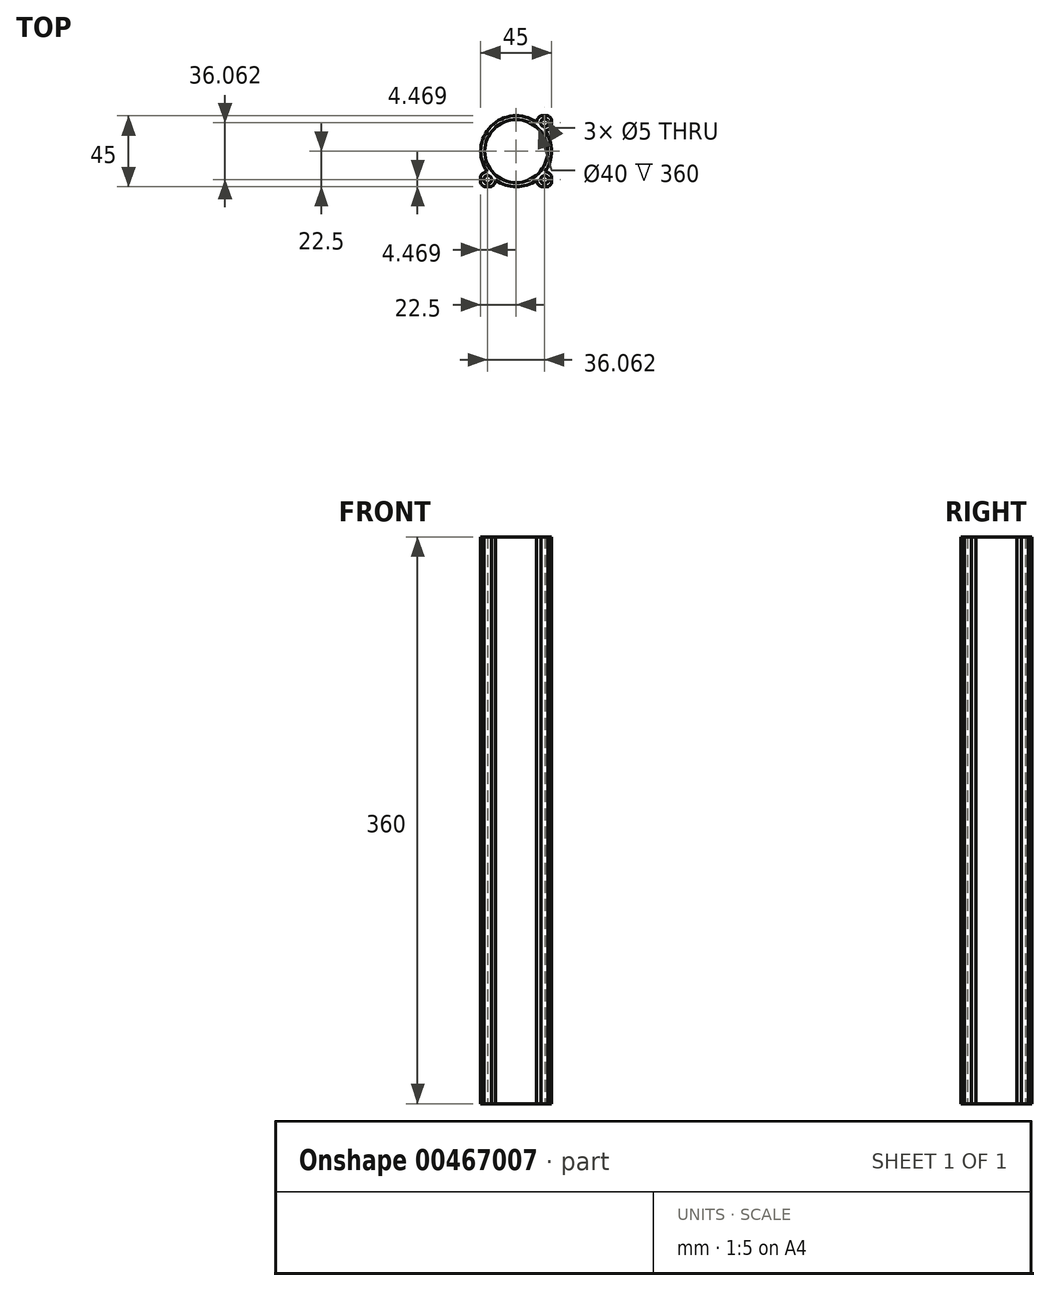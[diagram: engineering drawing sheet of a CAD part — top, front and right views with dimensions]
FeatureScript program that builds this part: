
annotation { "Feature Type Name" : "Feature", "Feature Type Description" : "" }
export const myFeature = defineFeature(function(context is Context, id is Id, definition is map)
    precondition{}
    {
        {
            var Q0;
            Q0=qCreatedBy(makeId("Top.planeOp"),FACE);
            var sketch = newSketch(context, id + "F0", { "sketchPlane" : qUnion([Q0])});
            skCircle(sketch, "E0", {"center": v(0, 0) * mm, "radius": 22.5 * mm});
            skLineSegment(sketch, "E1", {"start": v(0, 0) * mm, "end": v(22.5, 0) * mm});
            skLineSegment(sketch, "E2", {"start": v(22.5, 0) * mm, "end": v(22.5, 22.5) * mm});
            skLineSegment(sketch, "E3.bottom", {"start": v(22.5, 22.5) * mm, "end": v(-22.5, 22.5) * mm});
            skLineSegment(sketch, "E3.top", {"start": v(22.5, -22.5) * mm, "end": v(-22.5, -22.5) * mm});
            skLineSegment(sketch, "E3.left", {"start": v(22.5, 22.5) * mm, "end": v(22.5, -22.5) * mm});
            skLineSegment(sketch, "E3.right", {"start": v(-22.5, 22.5) * mm, "end": v(-22.5, -22.5) * mm});
            skLineSegment(sketch, "E4", {"start": v(-22.5, 22.5) * mm, "end": v(0, 0) * mm});
            skLineSegment(sketch, "E5", {"start": v(0, 0) * mm, "end": v(22.5, 22.5) * mm});
            skLineSegment(sketch, "E6", {"start": v(0, 0) * mm, "end": v(22.5, -22.5) * mm});
            skLineSegment(sketch, "E7", {"start": v(0, 0) * mm, "end": v(-22.5, -22.5) * mm});
            skLineSegment(sketch, "E8", {"start": v(-15.9, 15.9) * mm, "end": v(-18.03, 18.03) * mm});
            skCircle(sketch, "E9", {"center": v(-18.03, 18.03) * mm, "radius": 5 * mm});
            skCircle(sketch, "E10.MirrorC", {"center": v(18.03, -18.03) * mm, "radius": 5 * mm});
            skCircle(sketch, "E11.MirrorC", {"center": v(18.03, 18.03) * mm, "radius": 5 * mm});
            skCircle(sketch, "E12.MirrorC", {"center": v(-18.03, -18.03) * mm, "radius": 5 * mm});
            skSolve(sketch);
        }
        {
            var Q0;
            {var subQ6=sQuery(id+"F0.wireOp",EDGE,"E0");var subQ10=makeQuery(id+"F0.imprint","INTERSECT",VERTEX,{"derivedFrom":[subQ6,sQuery(id+"F0.wireOp",EDGE,"E3.right")]});Q0=makeQuery(id+"F0.imprint","IMPRINT",FACE,{"disambiguationData":[TD([[makeQuery(id+"F0.imprint","IMPRINT",EDGE,{"disambiguationData":[TD([[subQ10,1.0]])],"derivedFrom":subQ6}),1.0]])]});}
            var Q1;
            {var subQ7=sQuery(id+"F0.wireOp",EDGE,"E0");var subQ8=makeQuery(id+"F0.imprint","INTERSECT",VERTEX,{"derivedFrom":[subQ7,sQuery(id+"F0.wireOp",EDGE,"E3.bottom")]});Q1=makeQuery(id+"F0.imprint","IMPRINT",FACE,{"disambiguationData":[TD([[makeQuery(id+"F0.imprint","IMPRINT",EDGE,{"disambiguationData":[TD([[subQ8,1.0]])],"derivedFrom":subQ7}),1.0]])]});}
            var Q2;
            {var subQ0=sQuery(id+"F0.wireOp",EDGE,"E1");Q2=makeQuery(id+"F0.imprint","IMPRINT",FACE,{"disambiguationData":[TD([[makeQuery(id+"F0.imprint","IMPRINT",EDGE,{"derivedFrom":subQ0}),1.0]])]});}
            var Q3;
            {var subQ0=sQuery(id+"F0.wireOp",EDGE,"E1");Q3=makeQuery(id+"F0.imprint","IMPRINT",FACE,{"disambiguationData":[TD([[makeQuery(id+"F0.imprint","IMPRINT",EDGE,{"derivedFrom":subQ0}),-1.0]])]});}
            var Q4;
            {var subQ7=sQuery(id+"F0.wireOp",EDGE,"E0");var subQ8=makeQuery(id+"F0.imprint","INTERSECT",VERTEX,{"derivedFrom":[subQ7,sQuery(id+"F0.wireOp",EDGE,"E3.top")]});Q4=makeQuery(id+"F0.imprint","IMPRINT",FACE,{"disambiguationData":[TD([[makeQuery(id+"F0.imprint","IMPRINT",EDGE,{"disambiguationData":[TD([[subQ8,1.0]])],"derivedFrom":subQ7}),1.0]])]});}
            var Q5;
            {var subQ1=sQuery(id+"F0.wireOp",EDGE,"E0");var subQ3=sQuery(id+"F0.wireOp",EDGE,"E9");var subQ4=makeQuery(id+"F0.imprint","INTERSECT",VERTEX,{"disambiguationData":[OD(1.0)],"derivedFrom":[subQ1,subQ3]});Q5=makeQuery(id+"F0.imprint","IMPRINT",FACE,{"disambiguationData":[TD([[makeQuery(id+"F0.imprint","IMPRINT",EDGE,{"disambiguationData":[TD([[subQ4,-1.0]])],"derivedFrom":subQ3}),1.0]])]});}
            var Q6;
            {var subQ1=sQuery(id+"F0.wireOp",EDGE,"E0");var subQ3=sQuery(id+"F0.wireOp",EDGE,"E9");var subQ4=makeQuery(id+"F0.imprint","INTERSECT",VERTEX,{"disambiguationData":[OD(0.0)],"derivedFrom":[subQ1,subQ3]});Q6=makeQuery(id+"F0.imprint","IMPRINT",FACE,{"disambiguationData":[TD([[makeQuery(id+"F0.imprint","IMPRINT",EDGE,{"disambiguationData":[TD([[subQ4,1.0]])],"derivedFrom":subQ3}),1.0]])]});}
            var Q7;
            {var subQ0=sQuery(id+"F0.wireOp",EDGE,"E8");Q7=makeQuery(id+"F0.imprint","IMPRINT",FACE,{"disambiguationData":[TD([[makeQuery(id+"F0.imprint","IMPRINT",EDGE,{"derivedFrom":subQ0}),-1.0]])]});}
            var Q8;
            {var subQ0=sQuery(id+"F0.wireOp",EDGE,"E8");Q8=makeQuery(id+"F0.imprint","IMPRINT",FACE,{"disambiguationData":[TD([[makeQuery(id+"F0.imprint","IMPRINT",EDGE,{"derivedFrom":subQ0}),1.0]])]});}
            var Q9;
            {var subQ4=sQuery(id+"F0.wireOp",EDGE,"E5");var subQ6=sQuery(id+"F0.wireOp",EDGE,"E0");var subQ7=makeQuery(id+"F0.imprint","INTERSECT",VERTEX,{"derivedFrom":[subQ6,subQ4]});Q9=makeQuery(id+"F0.imprint","IMPRINT",FACE,{"disambiguationData":[TD([[makeQuery(id+"F0.imprint","IMPRINT",EDGE,{"disambiguationData":[TD([[subQ7,-1.0]])],"derivedFrom":subQ6}),-1.0]])]});}
            var Q10;
            {var subQ0=sQuery(id+"F0.wireOp",EDGE,"E11.MirrorC");var subQ3=sQuery(id+"F0.wireOp",EDGE,"E0");var subQ4=makeQuery(id+"F0.imprint","INTERSECT",VERTEX,{"disambiguationData":[OD(0.0)],"derivedFrom":[subQ3,subQ0]});Q10=makeQuery(id+"F0.imprint","IMPRINT",FACE,{"disambiguationData":[TD([[makeQuery(id+"F0.imprint","IMPRINT",EDGE,{"disambiguationData":[TD([[subQ4,-1.0]])],"derivedFrom":subQ3}),-1.0]])]});}
            var Q11;
            {var subQ0=sQuery(id+"F0.wireOp",EDGE,"E11.MirrorC");var subQ1=sQuery(id+"F0.wireOp",EDGE,"E0");var subQ2=makeQuery(id+"F0.imprint","INTERSECT",VERTEX,{"disambiguationData":[OD(0.0)],"derivedFrom":[subQ1,subQ0]});Q11=makeQuery(id+"F0.imprint","IMPRINT",FACE,{"disambiguationData":[TD([[makeQuery(id+"F0.imprint","IMPRINT",EDGE,{"disambiguationData":[TD([[subQ2,-1.0]])],"derivedFrom":subQ1}),1.0]])]});}
            var Q12;
            {var subQ0=sQuery(id+"F0.wireOp",EDGE,"E5");var subQ1=sQuery(id+"F0.wireOp",EDGE,"E0");var subQ2=makeQuery(id+"F0.imprint","INTERSECT",VERTEX,{"derivedFrom":[subQ1,subQ0]});Q12=makeQuery(id+"F0.imprint","IMPRINT",FACE,{"disambiguationData":[TD([[makeQuery(id+"F0.imprint","IMPRINT",EDGE,{"disambiguationData":[TD([[subQ2,-1.0]])],"derivedFrom":subQ1}),1.0]])]});}
            var Q13;
            {var subQ1=sQuery(id+"F0.wireOp",EDGE,"E0");var subQ3=sQuery(id+"F0.wireOp",EDGE,"E10.MirrorC");var subQ8=makeQuery(id+"F0.imprint","INTERSECT",VERTEX,{"disambiguationData":[OD(0.0)],"derivedFrom":[subQ1,subQ3]});Q13=makeQuery(id+"F0.imprint","IMPRINT",FACE,{"disambiguationData":[TD([[makeQuery(id+"F0.imprint","IMPRINT",EDGE,{"disambiguationData":[TD([[subQ8,-1.0]])],"derivedFrom":subQ1}),-1.0]])]});}
            var Q14;
            {var subQ3=sQuery(id+"F0.wireOp",EDGE,"E0");var subQ6=sQuery(id+"F0.wireOp",EDGE,"E6");var subQ7=makeQuery(id+"F0.imprint","INTERSECT",VERTEX,{"derivedFrom":[subQ3,subQ6]});Q14=makeQuery(id+"F0.imprint","IMPRINT",FACE,{"disambiguationData":[TD([[makeQuery(id+"F0.imprint","IMPRINT",EDGE,{"disambiguationData":[TD([[subQ7,-1.0]])],"derivedFrom":subQ3}),-1.0]])]});}
            var Q15;
            {var subQ0=sQuery(id+"F0.wireOp",EDGE,"E6");var subQ1=sQuery(id+"F0.wireOp",EDGE,"E0");var subQ2=makeQuery(id+"F0.imprint","INTERSECT",VERTEX,{"derivedFrom":[subQ1,subQ0]});Q15=makeQuery(id+"F0.imprint","IMPRINT",FACE,{"disambiguationData":[TD([[makeQuery(id+"F0.imprint","IMPRINT",EDGE,{"disambiguationData":[TD([[subQ2,-1.0]])],"derivedFrom":subQ1}),1.0]])]});}
            var Q16;
            {var subQ0=sQuery(id+"F0.wireOp",EDGE,"E10.MirrorC");var subQ1=sQuery(id+"F0.wireOp",EDGE,"E0");var subQ2=makeQuery(id+"F0.imprint","INTERSECT",VERTEX,{"disambiguationData":[OD(0.0)],"derivedFrom":[subQ1,subQ0]});Q16=makeQuery(id+"F0.imprint","IMPRINT",FACE,{"disambiguationData":[TD([[makeQuery(id+"F0.imprint","IMPRINT",EDGE,{"disambiguationData":[TD([[subQ2,-1.0]])],"derivedFrom":subQ1}),1.0]])]});}
            var Q17;
            {var subQ0=sQuery(id+"F0.wireOp",EDGE,"E12.MirrorC");var subQ5=sQuery(id+"F0.wireOp",EDGE,"E0");var subQ8=makeQuery(id+"F0.imprint","INTERSECT",VERTEX,{"disambiguationData":[OD(0.0)],"derivedFrom":[subQ5,subQ0]});Q17=makeQuery(id+"F0.imprint","IMPRINT",FACE,{"disambiguationData":[TD([[makeQuery(id+"F0.imprint","IMPRINT",EDGE,{"disambiguationData":[TD([[subQ8,-1.0]])],"derivedFrom":subQ5}),-1.0]])]});}
            var Q18;
            {var subQ3=sQuery(id+"F0.wireOp",EDGE,"E0");var subQ6=sQuery(id+"F0.wireOp",EDGE,"E7");var subQ7=makeQuery(id+"F0.imprint","INTERSECT",VERTEX,{"derivedFrom":[subQ3,subQ6]});Q18=makeQuery(id+"F0.imprint","IMPRINT",FACE,{"disambiguationData":[TD([[makeQuery(id+"F0.imprint","IMPRINT",EDGE,{"disambiguationData":[TD([[subQ7,-1.0]])],"derivedFrom":subQ3}),-1.0]])]});}
            var Q19;
            {var subQ0=sQuery(id+"F0.wireOp",EDGE,"E7");var subQ1=sQuery(id+"F0.wireOp",EDGE,"E0");var subQ2=makeQuery(id+"F0.imprint","INTERSECT",VERTEX,{"derivedFrom":[subQ1,subQ0]});Q19=makeQuery(id+"F0.imprint","IMPRINT",FACE,{"disambiguationData":[TD([[makeQuery(id+"F0.imprint","IMPRINT",EDGE,{"disambiguationData":[TD([[subQ2,-1.0]])],"derivedFrom":subQ1}),1.0]])]});}
            var Q20;
            {var subQ0=sQuery(id+"F0.wireOp",EDGE,"E12.MirrorC");var subQ1=sQuery(id+"F0.wireOp",EDGE,"E0");var subQ2=makeQuery(id+"F0.imprint","INTERSECT",VERTEX,{"disambiguationData":[OD(0.0)],"derivedFrom":[subQ1,subQ0]});Q20=makeQuery(id+"F0.imprint","IMPRINT",FACE,{"disambiguationData":[TD([[makeQuery(id+"F0.imprint","IMPRINT",EDGE,{"disambiguationData":[TD([[subQ2,-1.0]])],"derivedFrom":subQ1}),1.0]])]});}
            extrude(context, id + "F1", {"entities" : qUnion([Q0, Q1, Q2, Q3, Q4, Q5, Q6, Q7, Q8, Q9, Q10, Q11, Q12, Q13, Q14, Q15, Q16, Q17, Q18, Q19, Q20]), "depth" : 360 * mm, "offsetDistance" : 25 * mm});
        }
        {
            var Q0;
            Q0=makeQuery(id+"F1.opExtrude","CAP_FACE",FACE,{"disambiguationData":[OSD([sQuery(id+"F0.wireOp",EDGE,"E0"),sQuery(id+"F0.wireOp",EDGE,"E3.bottom"),sQuery(id+"F0.wireOp",EDGE,"E3.top"),sQuery(id+"F0.wireOp",EDGE,"E3.left"),sQuery(id+"F0.wireOp",EDGE,"E3.right"),sQuery(id+"F0.wireOp",EDGE,"E9"),sQuery(id+"F0.wireOp",EDGE,"E10.MirrorC"),sQuery(id+"F0.wireOp",EDGE,"E11.MirrorC"),sQuery(id+"F0.wireOp",EDGE,"E12.MirrorC")])],"isStart":false});
            var sketch = newSketch(context, id + "F2", { "sketchPlane" : qUnion([Q0])});
            skPoint(sketch, "E13", {"position": v(0, 0) * mm});
            skSolve(sketch);
        }
        {
            var Q0;
            Q0=sQuery(id+"F2.wireOp",VERTEX,"E13");
            var Q1;
            Q1=makeQuery(id+"F1.opExtrude","SWEPT_BODY",BODY,{"disambiguationData":[OSD([sQuery(id+"F0.wireOp",EDGE,"E0"),sQuery(id+"F0.wireOp",EDGE,"E3.bottom"),sQuery(id+"F0.wireOp",EDGE,"E3.top"),sQuery(id+"F0.wireOp",EDGE,"E3.left"),sQuery(id+"F0.wireOp",EDGE,"E3.right"),sQuery(id+"F0.wireOp",EDGE,"E9"),sQuery(id+"F0.wireOp",EDGE,"E10.MirrorC"),sQuery(id+"F0.wireOp",EDGE,"E11.MirrorC"),sQuery(id+"F0.wireOp",EDGE,"E12.MirrorC")])]});
            hole(context, id + "F3", {"style" : HoleStyle.SIMPLE, "endStyle" : HoleEndStyle.THROUGH, "holeDiameter" : 40 * mm, "isTappedThrough" : true, "tappedDepth" : 12 * mm, "tapClearance" : 3, "locations" : qUnion([Q0]), "scope" : qUnion([Q1])});
        }
        {
            var Q0;
            Q0=makeQuery(id+"F1.opExtrude","CAP_FACE",FACE,{"disambiguationData":[OSD([sQuery(id+"F0.wireOp",EDGE,"E0"),sQuery(id+"F0.wireOp",EDGE,"E3.bottom"),sQuery(id+"F0.wireOp",EDGE,"E3.top"),sQuery(id+"F0.wireOp",EDGE,"E3.left"),sQuery(id+"F0.wireOp",EDGE,"E3.right"),sQuery(id+"F0.wireOp",EDGE,"E9"),sQuery(id+"F0.wireOp",EDGE,"E10.MirrorC"),sQuery(id+"F0.wireOp",EDGE,"E11.MirrorC"),sQuery(id+"F0.wireOp",EDGE,"E12.MirrorC")])],"isStart":false});
            var sketch = newSketch(context, id + "F4", { "sketchPlane" : qUnion([Q0])});
            skPoint(sketch, "E14", {"position": v(-18.03, -18.03) * mm});
            skPoint(sketch, "E15", {"position": v(-18.03, 18.03) * mm});
            skPoint(sketch, "E16", {"position": v(18.03, 18.03) * mm});
            skPoint(sketch, "E17", {"position": v(18.03, -18.03) * mm});
            skSolve(sketch);
        }
        {
            var Q0;
            Q0=sQuery(id+"F4.wireOp",VERTEX,"E15");
            var Q1;
            Q1=sQuery(id+"F4.wireOp",VERTEX,"E16");
            var Q2;
            Q2=sQuery(id+"F4.wireOp",VERTEX,"E17");
            var Q3;
            Q3=sQuery(id+"F4.wireOp",VERTEX,"E14");
            var Q4;
            Q4=makeQuery(id+"F1.opExtrude","SWEPT_BODY",BODY,{"disambiguationData":[OSD([sQuery(id+"F0.wireOp",EDGE,"E0"),sQuery(id+"F0.wireOp",EDGE,"E3.bottom"),sQuery(id+"F0.wireOp",EDGE,"E3.top"),sQuery(id+"F0.wireOp",EDGE,"E3.left"),sQuery(id+"F0.wireOp",EDGE,"E3.right"),sQuery(id+"F0.wireOp",EDGE,"E9"),sQuery(id+"F0.wireOp",EDGE,"E10.MirrorC"),sQuery(id+"F0.wireOp",EDGE,"E11.MirrorC"),sQuery(id+"F0.wireOp",EDGE,"E12.MirrorC")])]});
            hole(context, id + "F5", {"style" : HoleStyle.SIMPLE, "endStyle" : HoleEndStyle.THROUGH, "holeDiameter" : 5 * mm, "isTappedThrough" : true, "tappedDepth" : 12 * mm, "tapClearance" : 3, "locations" : qUnion([Q0, Q1, Q2, Q3]), "scope" : qUnion([Q4])});
        }
    });
